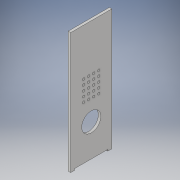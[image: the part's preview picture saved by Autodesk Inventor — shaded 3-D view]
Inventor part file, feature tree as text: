
AUTODESK INVENTOR PART (.ipt)
format: ipt  version: 2019 (Build 230136000, 136)  size: 140,288 bytes
history: native  units: mm
features: sketch x2, extrude x1
ambient origin geometry x8: Origin, YZ Plane, XZ Plane, XY Plane, X Axis, Y Axis, Z Axis, Center Point
bodies: Solid1 (feature_tree)
feature tree (3):
  sketch  "Sketch1"  dims[d0=241.0mm d1=82.0mm]
  sketch  "Sketch2"  dims[d2=38.0mm d3=41.0mm d4=174.0mm d5=66.0mm d6=3.0mm d7=8.0mm d21=4.7mm d22=50.0mm d24=10.0mm d25=40.0mm d27=10.0mm d32=5.0mm d33=0.0mm]
  extrude  "Extrusion1"  Depth=82.0mm
